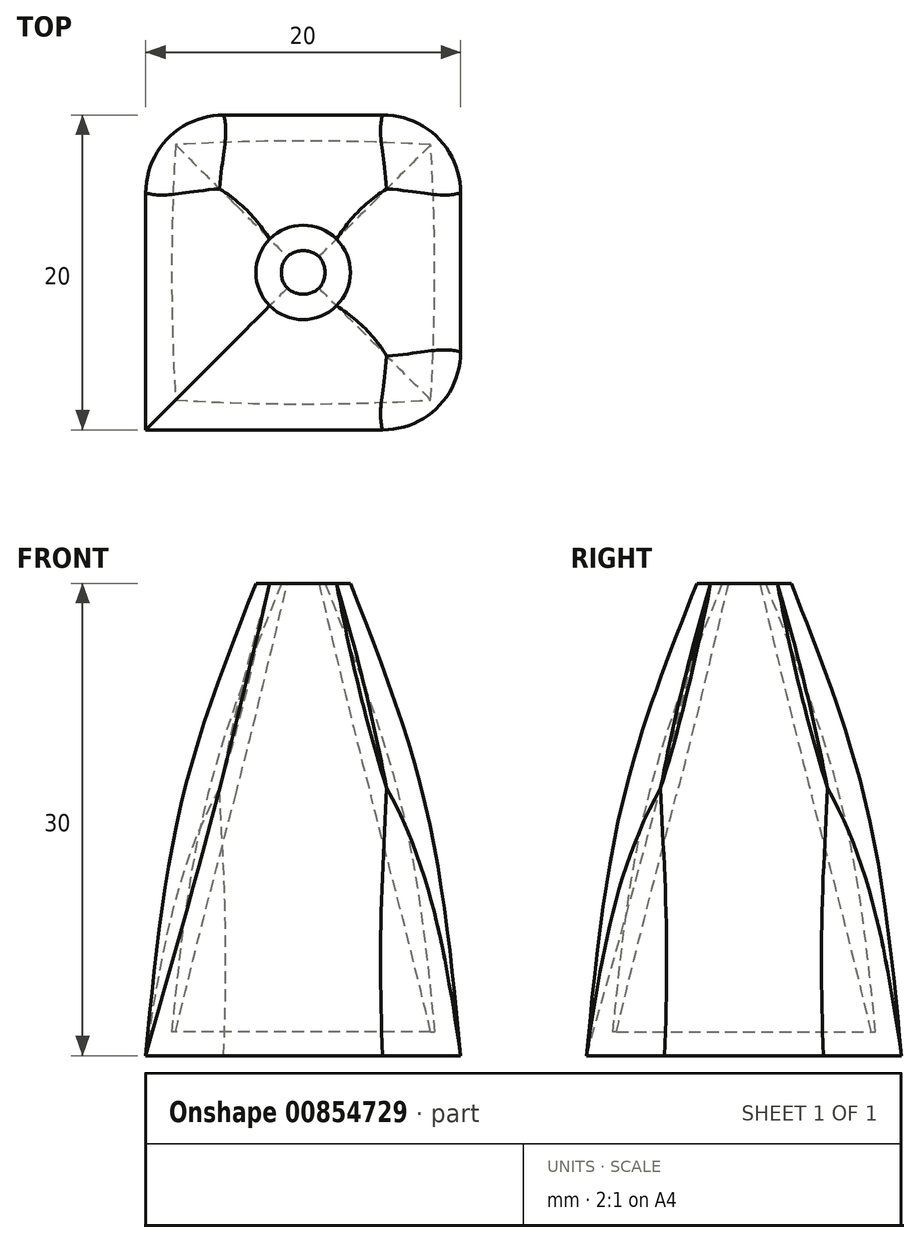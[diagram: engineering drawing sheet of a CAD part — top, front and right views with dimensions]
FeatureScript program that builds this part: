
annotation { "Feature Type Name" : "Feature", "Feature Type Description" : "" }
export const myFeature = defineFeature(function(context is Context, id is Id, definition is map)
    precondition{}
    {
        {
            var Q0;
            Q0=qCreatedBy(makeId("Top.planeOp"),FACE);
            var sketch = newSketch(context, id + "F0", { "sketchPlane" : qUnion([Q0])});
            skLineSegment(sketch, "E0.bottom", {"start": v(-10, 10) * mm, "end": v(10, 10) * mm});
            skLineSegment(sketch, "E0.top", {"start": v(-10, -10) * mm, "end": v(10, -10) * mm});
            skLineSegment(sketch, "E0.left", {"start": v(-10, 10) * mm, "end": v(-10, -10) * mm});
            skLineSegment(sketch, "E0.right", {"start": v(10, 10) * mm, "end": v(10, -10) * mm});
            skPoint(sketch, "E0.middle", {"position": v(0, 0) * mm});
            skSolve(sketch);
        }
        {
            var Q0;
            Q0=qCreatedBy(makeId("Top.planeOp"),FACE);
            cPlane(context, id + "F1", {"entities" : qUnion([Q0]), "cplaneType" : CPlaneType.OFFSET, "offset" : 17 * mm, "width" : 150 * mm, "height" : 150 * mm});
        }
        {
            var Q0;
            Q0=qCreatedBy(id+"F1.planeOp",FACE);
            var sketch = newSketch(context, id + "F2", { "sketchPlane" : qUnion([Q0])});
            skCircle(sketch, "E1", {"center": v(0, 0) * mm, "radius": 7.5 * mm});
            skSolve(sketch);
        }
        {
            var Q0;
            Q0=qCreatedBy(id+"F1.planeOp",FACE);
            cPlane(context, id + "F3", {"entities" : qUnion([Q0]), "cplaneType" : CPlaneType.OFFSET, "offset" : 13 * mm, "width" : 150 * mm, "height" : 150 * mm});
        }
        {
            var Q0;
            Q0=qCreatedBy(id+"F3.planeOp",FACE);
            var sketch = newSketch(context, id + "F4", { "sketchPlane" : qUnion([Q0])});
            skCircle(sketch, "E2", {"center": v(0, 0) * mm, "radius": 3 * mm});
            skSolve(sketch);
        }
        {
            var Q0;
            Q0=makeQuery(id+"F0.imprint","IMPRINT",FACE,{"disambiguationData":[TD([[makeQuery(id+"F0.imprint","IMPRINT",EDGE,{"derivedFrom":sQuery(id+"F0.wireOp",EDGE,"E0.bottom")}),-1.0]])]});
            var Q1;
            Q1=makeQuery(id+"F2.imprint","IMPRINT",FACE,{"disambiguationData":[TD([[makeQuery(id+"F2.imprint","IMPRINT",EDGE,{"derivedFrom":sQuery(id+"F2.wireOp",EDGE,"E1")}),1.0]])]});
            var Q2;
            Q2=makeQuery(id+"F4.imprint","IMPRINT",FACE,{"disambiguationData":[TD([[makeQuery(id+"F4.imprint","IMPRINT",EDGE,{"derivedFrom":sQuery(id+"F4.wireOp",EDGE,"E2")}),1.0]])]});
            loft(context, id + "F5", {"sheetProfilesArray" : [{ "sheetProfileEntities" : qUnion([Q0]) }, { "sheetProfileEntities" : qUnion([Q1]) }, { "sheetProfileEntities" : qUnion([Q2]) }]});
        }
        {
            var Q0;
            Q0=makeQuery(id+"F5.opLoft","CAP_FACE",FACE,{"disambiguationData":[OSD([makeQuery(id+"F4.imprint","IMPRINT",FACE,{"disambiguationData":[TD([[makeQuery(id+"F4.imprint","IMPRINT",EDGE,{"derivedFrom":sQuery(id+"F4.wireOp",EDGE,"E2")}),1.0]])]})])],"isStart":true});
            shell(context, id + "F6", {"entities" : qUnion([Q0]), "thickness" : 1.5 * mm});
        }
        {
            var Q0;
            Q0=makeQuery(id+"F5.opLoft","SWEPT_EDGE",EDGE,{"disambiguationData":[OSD([sQuery(id+"F0.wireOp",EDGE,"E0.top"),sQuery(id+"F0.wireOp",EDGE,"E0.left"),sQuery(id+"F0.wireOp",EDGE,"E0.right"),sQuery(id+"F2.wireOp",EDGE,"E1"),sQuery(id+"F4.wireOp",EDGE,"E2")])]});
            var Q1;
            Q1=makeQuery(id+"F5.opLoft","SWEPT_EDGE",EDGE,{"disambiguationData":[OSD([sQuery(id+"F0.wireOp",EDGE,"E0.bottom"),sQuery(id+"F0.wireOp",EDGE,"E0.top"),sQuery(id+"F0.wireOp",EDGE,"E0.right"),sQuery(id+"F2.wireOp",EDGE,"E1"),sQuery(id+"F4.wireOp",EDGE,"E2")])]});
            var Q2;
            Q2=makeQuery(id+"F5.opLoft","SWEPT_EDGE",EDGE,{"disambiguationData":[OSD([sQuery(id+"F0.wireOp",EDGE,"E0.bottom"),sQuery(id+"F0.wireOp",EDGE,"E0.left")])]});
            var Q3;
            Q3=makeQuery(id+"F5.opLoft","SWEPT_EDGE",EDGE,{"disambiguationData":[OSD([sQuery(id+"F0.wireOp",EDGE,"E0.bottom"),sQuery(id+"F0.wireOp",EDGE,"E0.top"),sQuery(id+"F0.wireOp",EDGE,"E0.left"),sQuery(id+"F2.wireOp",EDGE,"E1"),sQuery(id+"F4.wireOp",EDGE,"E2")])]});
            fillet(context, id + "F7", {"entities" : qUnion([Q0, Q1, Q2, Q3]), "radius" : 5 * mm, "tangentPropagation" : true, "allowEdgeOverflow" : false});
        }
    });
